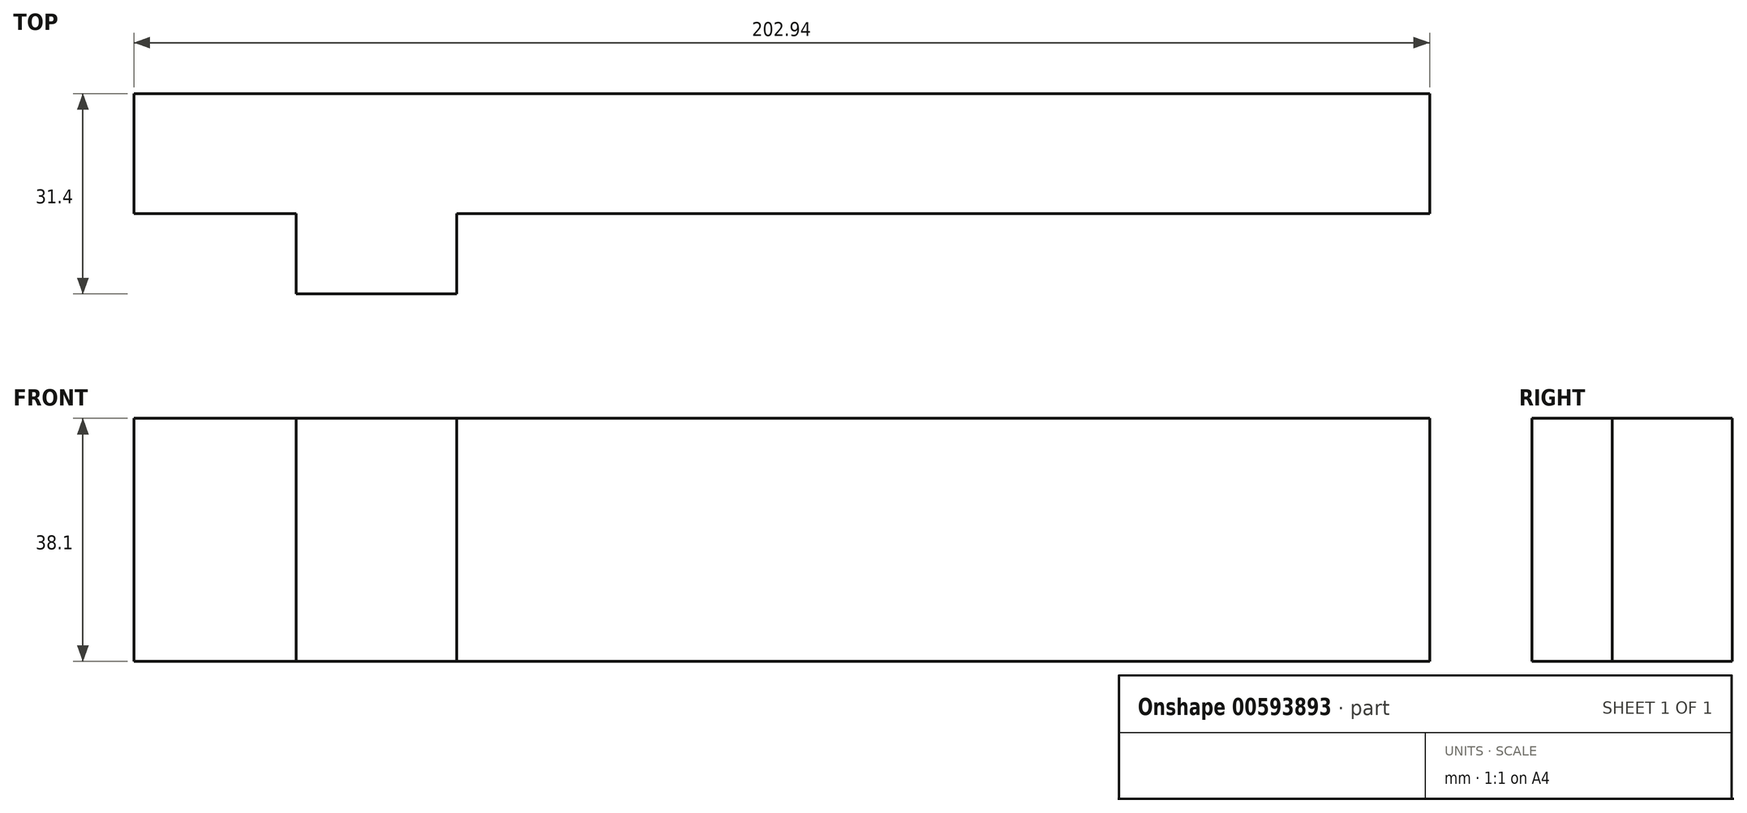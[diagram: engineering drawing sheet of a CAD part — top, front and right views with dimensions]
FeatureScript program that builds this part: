
annotation { "Feature Type Name" : "Feature", "Feature Type Description" : "" }
export const myFeature = defineFeature(function(context is Context, id is Id, definition is map)
    precondition{}
    {
        {
            var Q0;
            Q0=qCreatedBy(makeId("Top.planeOp"),FACE);
            var sketch = newSketch(context, id + "F0", { "sketchPlane" : qUnion([Q0])});
            skLineSegment(sketch, "E0", {"start": v(-36.97, 14.28) * mm, "end": v(38.97, 14.28) * mm});
            skLineSegment(sketch, "E1", {"start": v(38.97, 14.28) * mm, "end": v(38.97, -4.52) * mm});
            skLineSegment(sketch, "E2", {"start": v(38.97, -4.52) * mm, "end": v(13.57, -4.52) * mm});
            skLineSegment(sketch, "E3", {"start": v(13.57, -4.52) * mm, "end": v(13.57, -17.12) * mm});
            skLineSegment(sketch, "E4", {"start": v(13.57, -17.12) * mm, "end": v(-11.57, -17.12) * mm});
            skLineSegment(sketch, "E5", {"start": v(-11.57, -17.12) * mm, "end": v(-11.57, -4.52) * mm});
            skLineSegment(sketch, "E6", {"start": v(-11.57, -4.52) * mm, "end": v(-36.97, -4.52) * mm});
            skLineSegment(sketch, "E7", {"start": v(-36.97, -4.52) * mm, "end": v(-36.97, 14.28) * mm});
            skSolve(sketch);
        }
        {
            var Q0;
            Q0=makeQuery(id+"F0.imprint","IMPRINT",FACE,{"disambiguationData":[TD([[makeQuery(id+"F0.imprint","IMPRINT",EDGE,{"derivedFrom":sQuery(id+"F0.wireOp",EDGE,"E0")}),-1.0]])]});
            extrude(context, id + "F1", {"entities" : qUnion([Q0]), "depth" : 38.1 * mm, "offsetDistance" : 25.4 * mm});
        }
        {
            var Q0;
            Q0=makeQuery(id+"F1.opExtrude","SWEPT_FACE",FACE,{"disambiguationData":[OSD([sQuery(id+"F0.wireOp",EDGE,"E1")])]});
            var sketch = newSketch(context, id + "F2", { "sketchPlane" : qUnion([Q0])});
            skLineSegment(sketch, "E8.bottom", {"start": v(-4.52, 38.1) * mm, "end": v(14.28, 38.1) * mm});
            skLineSegment(sketch, "E8.top", {"start": v(-4.52, 0) * mm, "end": v(14.28, 0) * mm});
            skLineSegment(sketch, "E8.left", {"start": v(-4.52, 38.1) * mm, "end": v(-4.52, 0) * mm});
            skLineSegment(sketch, "E8.right", {"start": v(14.28, 38.1) * mm, "end": v(14.28, 0) * mm});
            skSolve(sketch);
        }
        {
            var Q0;
            Q0=makeQuery(id+"F2.imprint","IMPRINT",FACE,{"disambiguationData":[TD([[makeQuery(id+"F2.imprint","IMPRINT",EDGE,{"derivedFrom":sQuery(id+"F2.wireOp",EDGE,"E8.bottom")}),1.0]])]});
            extrude(context, id + "F3", {"entities" : qUnion([Q0]), "operationType" : NewBodyOperationType.ADD, "depth" : 127 * mm, "offsetDistance" : 25.4 * mm});
        }
    });
